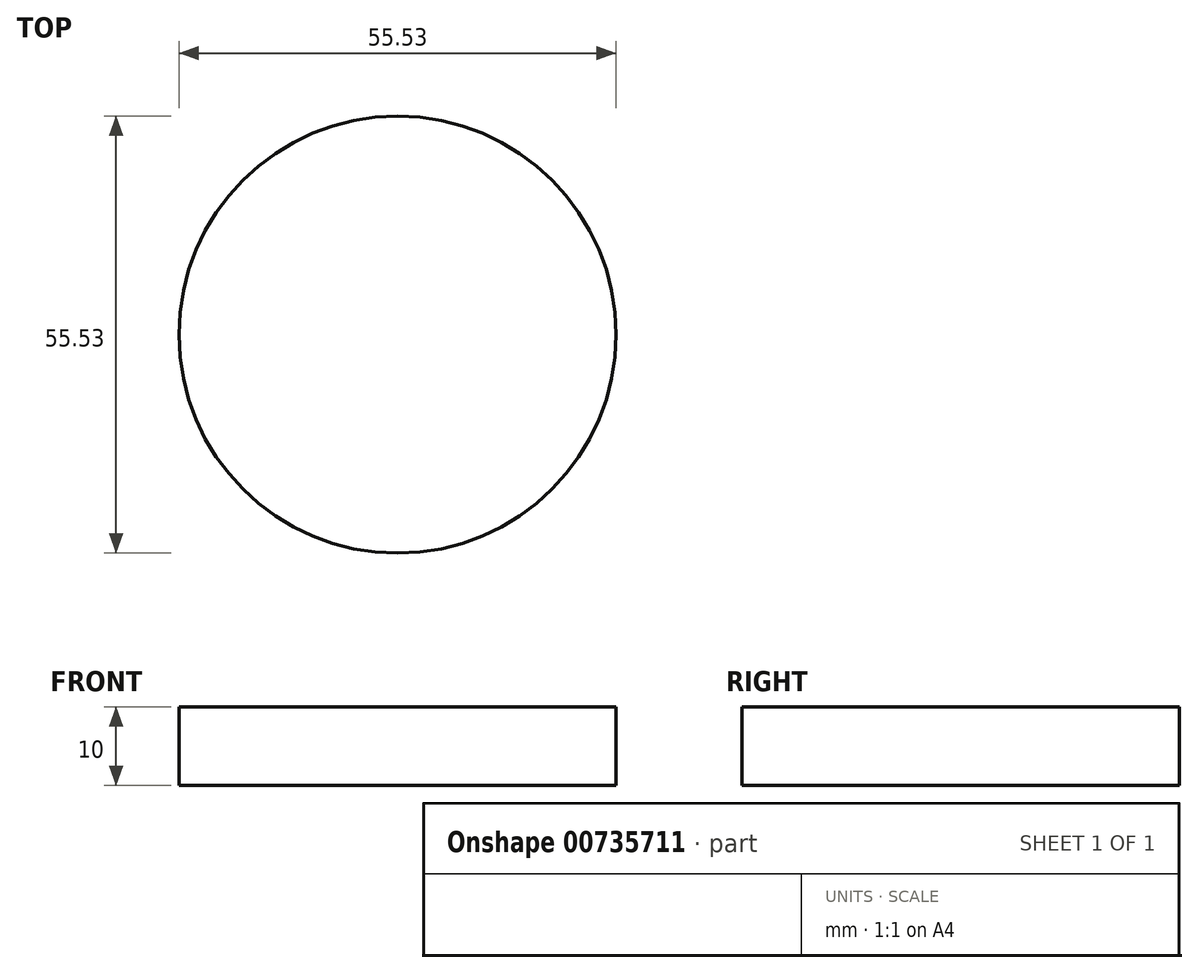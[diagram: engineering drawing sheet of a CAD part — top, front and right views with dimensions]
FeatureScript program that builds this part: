
annotation { "Feature Type Name" : "Feature", "Feature Type Description" : "" }
export const myFeature = defineFeature(function(context is Context, id is Id, definition is map)
    precondition{}
    {
        {
            var Q0;
            Q0=qCreatedBy(makeId("Top.planeOp"),FACE);
            var sketch = newSketch(context, id + "F0", { "sketchPlane" : qUnion([Q0])});
            skCircle(sketch, "E0", {"center": v(-39.8, 32.63) * mm, "radius": 27.76 * mm});
            skSolve(sketch);
        }
        {
            var Q0;
            Q0=qSketchRegion(id+"F0",true);
            extrude(context, id + "F1", {"entities" : qUnion([Q0]), "depth" : 10 * mm, "offsetDistance" : 25.4 * mm});
        }
    });
